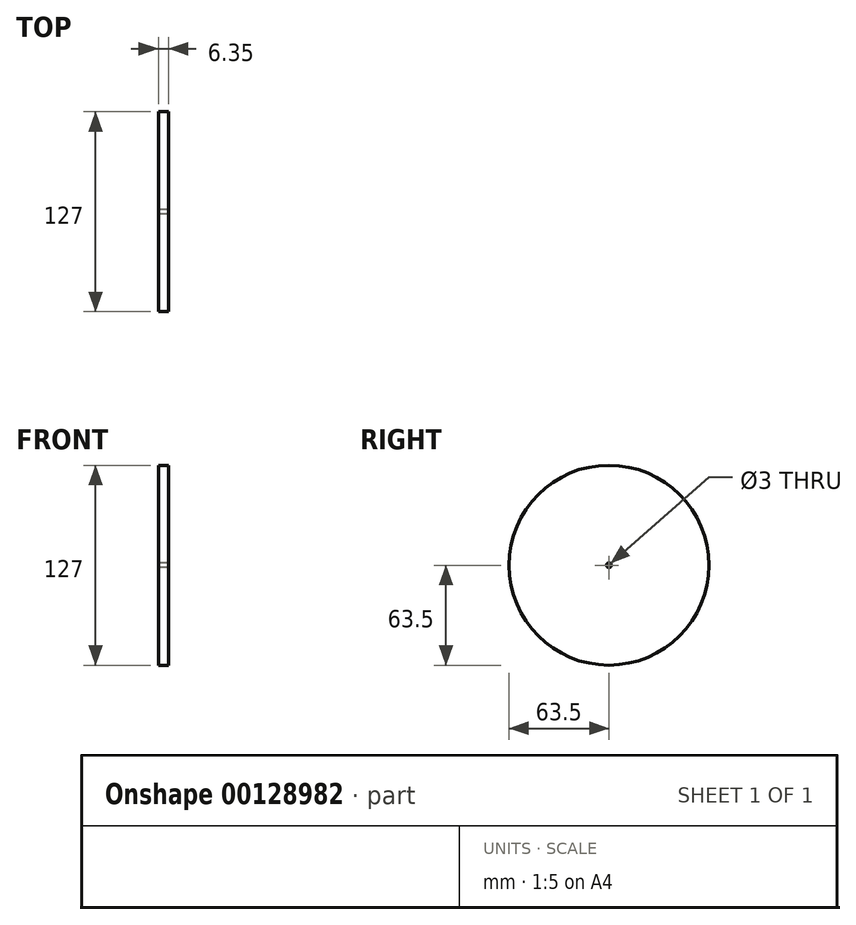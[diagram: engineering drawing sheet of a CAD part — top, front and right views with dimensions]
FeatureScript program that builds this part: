
annotation { "Feature Type Name" : "Feature", "Feature Type Description" : "" }
export const myFeature = defineFeature(function(context is Context, id is Id, definition is map)
    precondition{}
    {
        {
            var Q0;
            Q0=qCreatedBy(makeId("Right.planeOp"),FACE);
            var sketch = newSketch(context, id + "F0", { "sketchPlane" : qUnion([Q0])});
            skCircle(sketch, "E0", {"center": v(0, 0) * mm, "radius": 63.5 * mm});
            skSolve(sketch);
        }
        {
            var Q0;
            Q0=makeQuery(id+"F0.imprint","IMPRINT",FACE,{"disambiguationData":[TD([[makeQuery(id+"F0.imprint","IMPRINT",EDGE,{"derivedFrom":sQuery(id+"F0.wireOp",EDGE,"E0")}),1.0]])]});
            extrude(context, id + "F1", {"entities" : qUnion([Q0]), "depth" : 6.35 * mm});
        }
        {
            var Q0;
            Q0=sQuery(id+"F0.wireOp",VERTEX,"E0.center");
            var Q1;
            Q1=makeQuery(id+"F1.opExtrude","SWEPT_BODY",BODY,{"disambiguationData":[OSD([sQuery(id+"F0.wireOp",EDGE,"E0")])]});
            hole(context, id + "F2", {"style" : HoleStyle.SIMPLE, "endStyle" : HoleEndStyle.THROUGH, "oppositeDirection" : true, "holeDiameter" : 3 * mm, "locations" : qUnion([Q0]), "scope" : qUnion([Q1]), "isTappedThrough" : true});
        }
    });
